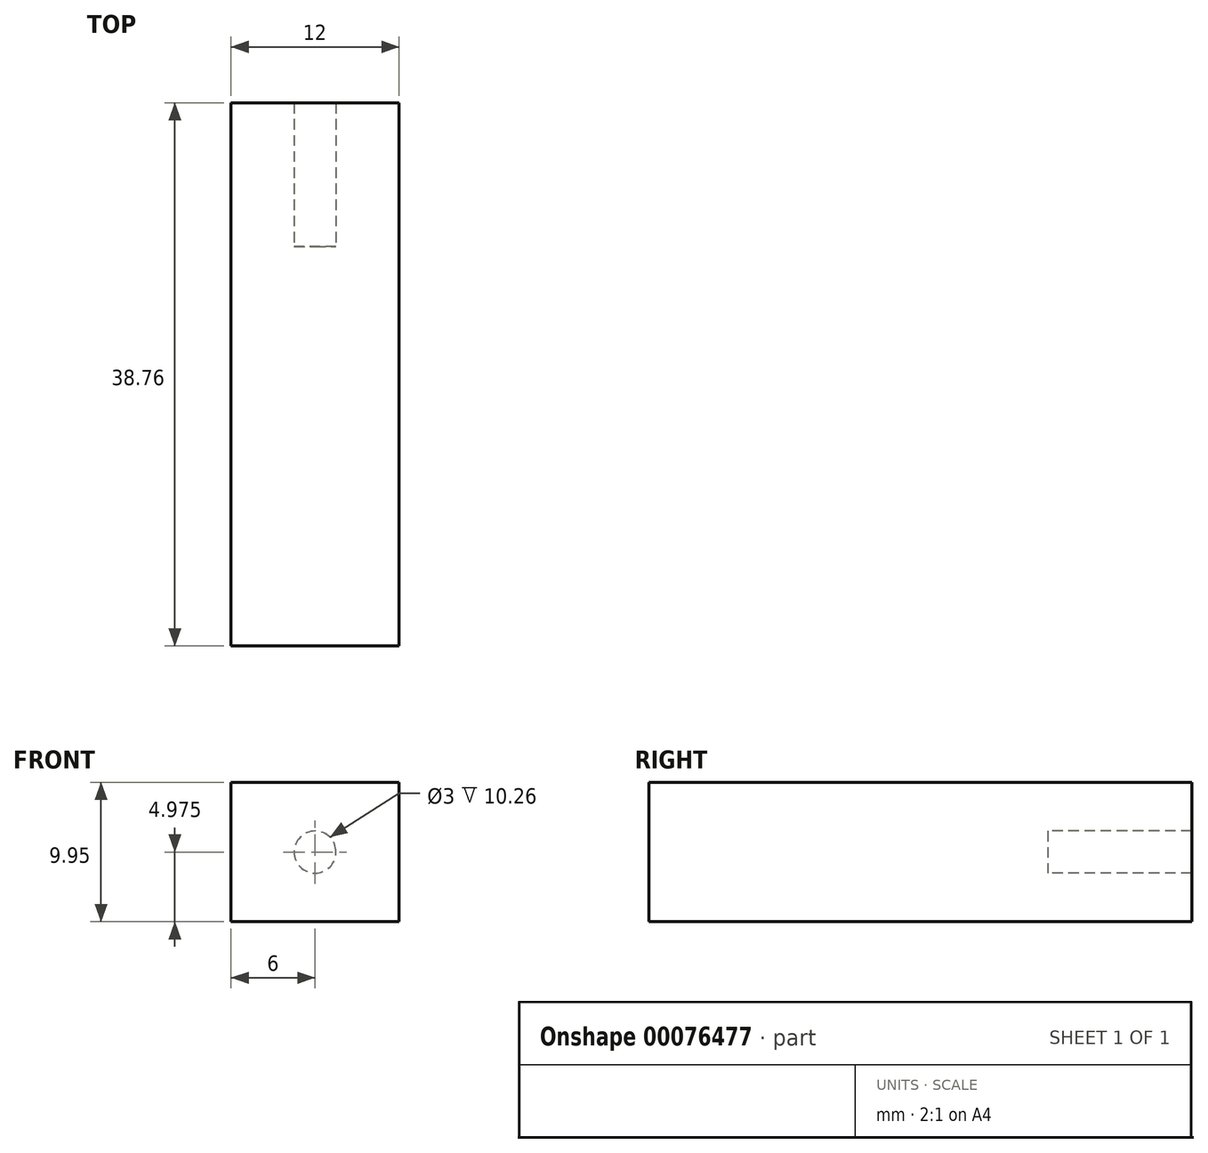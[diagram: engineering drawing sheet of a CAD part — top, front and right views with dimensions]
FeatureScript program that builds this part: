
annotation { "Feature Type Name" : "Feature", "Feature Type Description" : "" }
export const myFeature = defineFeature(function(context is Context, id is Id, definition is map)
    precondition{}
    {
        {
            var Q0;
            Q0=qCreatedBy(makeId("Front.planeOp"),FACE);
            var sketch = newSketch(context, id + "F0", { "sketchPlane" : qUnion([Q0])});
            skLineSegment(sketch, "E0.bottom", {"start": v(-6, 9.95) * mm, "end": v(6, 9.95) * mm});
            skLineSegment(sketch, "E0.top", {"start": v(-6, 0) * mm, "end": v(6, 0) * mm});
            skLineSegment(sketch, "E0.left", {"start": v(-6, 9.95) * mm, "end": v(-6, 0) * mm});
            skLineSegment(sketch, "E0.right", {"start": v(6, 9.95) * mm, "end": v(6, 0) * mm});
            skSolve(sketch);
        }
        {
            var Q0;
            Q0=makeQuery(id+"F0.imprint","IMPRINT",FACE,{"disambiguationData":[TD([[makeQuery(id+"F0.imprint","IMPRINT",EDGE,{"derivedFrom":sQuery(id+"F0.wireOp",EDGE,"E0.bottom")}),-1.0]])]});
            extrude(context, id + "F1", {"entities" : qUnion([Q0]), "depth" : 28.5 * mm});
        }
        {
            var Q0;
            Q0=makeQuery(id+"F1.opExtrude","CAP_FACE",FACE,{"disambiguationData":[OSD([sQuery(id+"F0.wireOp",EDGE,"E0.bottom"),sQuery(id+"F0.wireOp",EDGE,"E0.top"),sQuery(id+"F0.wireOp",EDGE,"E0.left"),sQuery(id+"F0.wireOp",EDGE,"E0.right")])],"isStart":true});
            var sketch = newSketch(context, id + "F2", { "sketchPlane" : qUnion([Q0])});
            skLineSegment(sketch, "E1", {"start": v(0, 0) * mm, "end": v(0, 9.95) * mm});
            skCircle(sketch, "E2", {"center": v(0, 4.97) * mm, "radius": 1.5 * mm});
            skSolve(sketch);
        }
        {
            var Q0;
            {var subQ0=sQuery(id+"F2.wireOp",EDGE,"E2");var subQ1=sQuery(id+"F2.wireOp",EDGE,"E1");var subQ2=makeQuery(id+"F2.imprint","INTERSECT",VERTEX,{"disambiguationData":[OD(0.0)],"derivedFrom":[subQ1,subQ0]});Q0=makeQuery(id+"F2.imprint","IMPRINT",FACE,{"disambiguationData":[TD([[makeQuery(id+"F2.imprint","IMPRINT",EDGE,{"disambiguationData":[TD([[subQ2,-1.0]])],"derivedFrom":subQ1}),1.0]])]});}
            var Q1;
            {var subQ0=sQuery(id+"F2.wireOp",EDGE,"E2");var subQ1=sQuery(id+"F2.wireOp",EDGE,"E1");var subQ2=makeQuery(id+"F2.imprint","INTERSECT",VERTEX,{"disambiguationData":[OD(0.0)],"derivedFrom":[subQ1,subQ0]});Q1=makeQuery(id+"F2.imprint","IMPRINT",FACE,{"disambiguationData":[TD([[makeQuery(id+"F2.imprint","IMPRINT",EDGE,{"disambiguationData":[TD([[subQ2,-1.0]])],"derivedFrom":subQ1}),-1.0]])]});}
            extrude(context, id + "F3", {"entities" : qUnion([Q0, Q1]), "operationType" : NewBodyOperationType.ADD, "depth" : 10.26 * mm});
        }
    });
